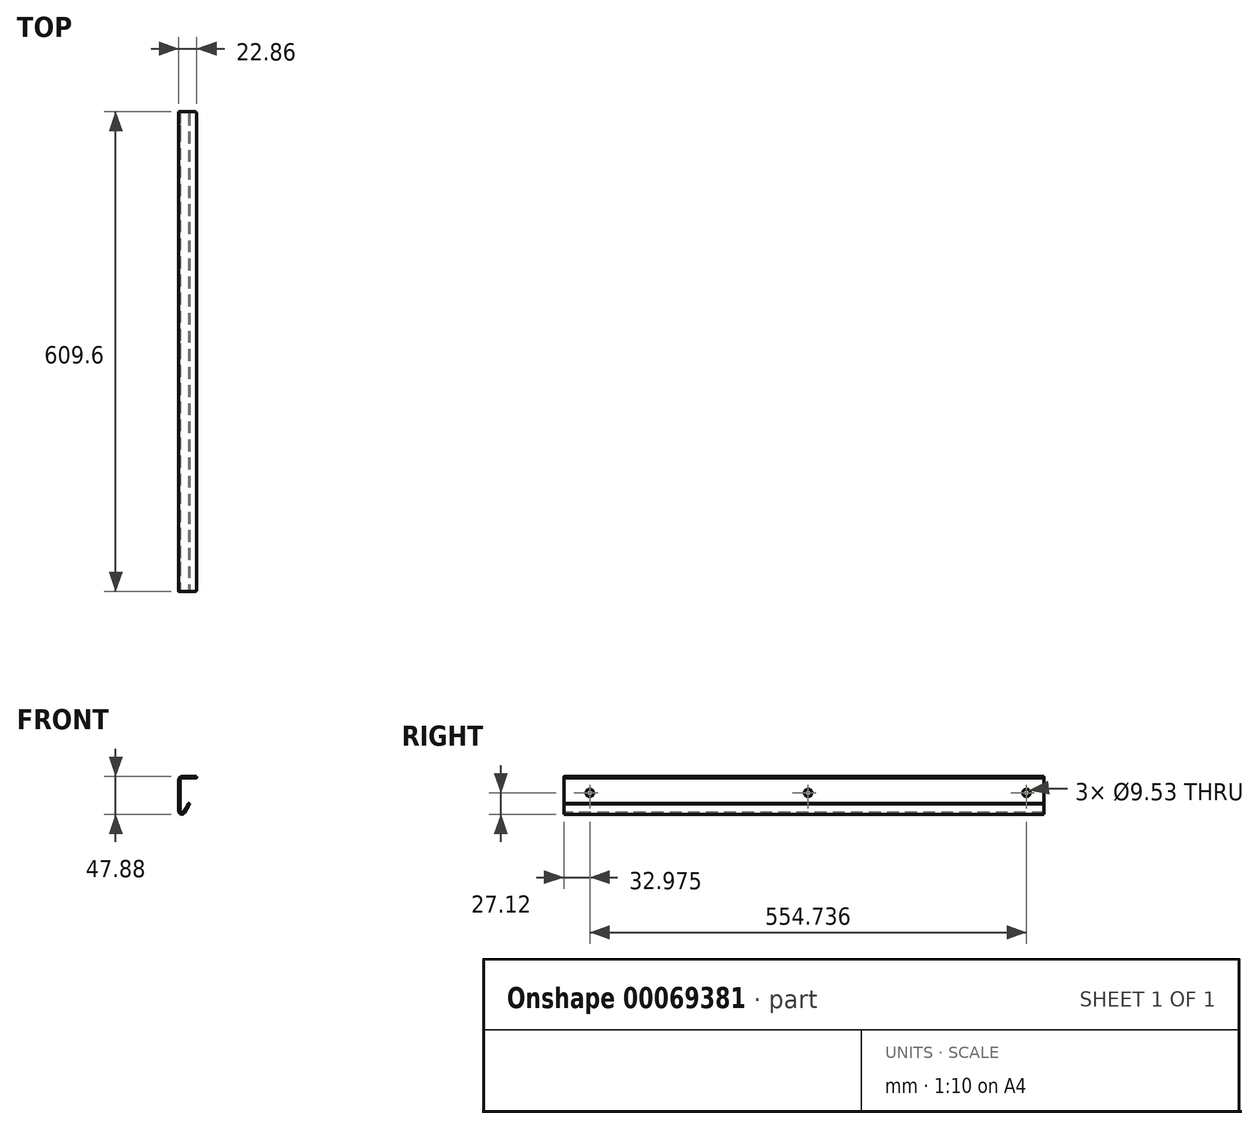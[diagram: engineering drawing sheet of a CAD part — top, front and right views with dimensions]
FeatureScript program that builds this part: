
annotation { "Feature Type Name" : "Feature", "Feature Type Description" : "" }
export const myFeature = defineFeature(function(context is Context, id is Id, definition is map)
    precondition{}
    {
        {
            var Q0;
            Q0=qCreatedBy(makeId("Front.planeOp"),FACE);
            var sketch = newSketch(context, id + "F0", { "sketchPlane" : qUnion([Q0])});
            skLineSegment(sketch, "E0", {"start": v(-1.41, 19.26) * mm, "end": v(-20.23, 19.26) * mm});
            skLineSegment(sketch, "E1", {"start": v(-22.77, 16.72) * mm, "end": v(-22.77, -22.45) * mm});
            skLineSegment(sketch, "E2", {"start": v(-18.03, -23.72) * mm, "end": v(-12.11, -13.47) * mm});
            skLineSegment(sketch, "E3.0", {"start": v(-17.16, -25.21) * mm, "end": v(-10.81, -14.21) * mm});
            skLineSegment(sketch, "E3.1", {"start": v(-24.27, 16.95) * mm, "end": v(-24.27, -23.3) * mm});
            skLineSegment(sketch, "E3.2", {"start": v(-1.41, 20.76) * mm, "end": v(-20.46, 20.76) * mm});
            skLineSegment(sketch, "E4", {"start": v(-10.81, -14.21) * mm, "end": v(-12.11, -13.47) * mm});
            skLineSegment(sketch, "E5", {"start": v(-1.41, 20.76) * mm, "end": v(-1.41, 19.26) * mm});
            skPoint(sketch, "E6.visualSharp", {"position": v(-22.77, 19.26) * mm});
            skArc(sketch, "E6.filletArc", {"start": v(-20.23, 19.26) * mm, "mid": v(-22.03, 18.52) * mm, "end": v(-22.77, 16.72) * mm});
            skPoint(sketch, "E7.visualSharp", {"position": v(-22.77, -31.93) * mm});
            skArc(sketch, "E7.filletArc", {"start": v(-22.77, -22.45) * mm, "mid": v(-20.9, -24.9) * mm, "end": v(-18.03, -23.72) * mm});
            skPoint(sketch, "E8.visualSharp", {"position": v(-24.27, -37.53) * mm});
            skArc(sketch, "E8.filletArc", {"start": v(-24.27, -23.3) * mm, "mid": v(-21.45, -26.99) * mm, "end": v(-17.16, -25.21) * mm});
            skPoint(sketch, "E9.visualSharp", {"position": v(-24.27, 20.76) * mm});
            skArc(sketch, "E9.filletArc", {"start": v(-20.46, 20.76) * mm, "mid": v(-23.16, 19.64) * mm, "end": v(-24.27, 16.95) * mm});
            skSolve(sketch);
        }
        {
            var Q0;
            Q0=qSketchRegion(id+"F0",true);
            extrude(context, id + "F1", {"entities" : qUnion([Q0]), "oppositeDirection" : true, "depth" : 609.6 * mm});
        }
        {
            var Q0;
            Q0=makeQuery(id+"F1.opExtrude","SWEPT_FACE",FACE,{"disambiguationData":[OSD([sQuery(id+"F0.wireOp",EDGE,"E3.2")])]});
            var sketch = newSketch(context, id + "F2", { "sketchPlane" : qUnion([Q0])});
            skCircle(sketch, "E10", {"center": v(-14.11, 12.7) * mm, "radius": 3.18 * mm});
            skCircle(sketch, "E11.0.1.0", {"center": v(-14.11, 38.1) * mm, "radius": 3.18 * mm});
            skCircle(sketch, "E11.0.2.0", {"center": v(-14.11, 63.5) * mm, "radius": 3.18 * mm});
            skCircle(sketch, "E11.0.3.0", {"center": v(-14.11, 88.9) * mm, "radius": 3.18 * mm});
            skCircle(sketch, "E11.0.4.0", {"center": v(-14.11, 114.3) * mm, "radius": 3.18 * mm});
            skCircle(sketch, "E11.0.5.0", {"center": v(-14.11, 139.7) * mm, "radius": 3.18 * mm});
            skCircle(sketch, "E11.0.6.0", {"center": v(-14.11, 165.1) * mm, "radius": 3.18 * mm});
            skCircle(sketch, "E11.0.7.0", {"center": v(-14.11, 190.5) * mm, "radius": 3.18 * mm});
            skCircle(sketch, "E11.0.8.0", {"center": v(-14.11, 215.9) * mm, "radius": 3.18 * mm});
            skCircle(sketch, "E11.0.9.0", {"center": v(-14.11, 241.3) * mm, "radius": 3.18 * mm});
            skCircle(sketch, "E11.0.10.0", {"center": v(-14.11, 266.7) * mm, "radius": 3.18 * mm});
            skCircle(sketch, "E11.0.11.0", {"center": v(-14.11, 292.1) * mm, "radius": 3.18 * mm});
            skCircle(sketch, "E11.0.12.0", {"center": v(-14.11, 317.5) * mm, "radius": 3.18 * mm});
            skCircle(sketch, "E11.0.13.0", {"center": v(-14.11, 342.9) * mm, "radius": 3.18 * mm});
            skCircle(sketch, "E11.0.14.0", {"center": v(-14.11, 368.3) * mm, "radius": 3.18 * mm});
            skCircle(sketch, "E11.0.15.0", {"center": v(-14.11, 393.7) * mm, "radius": 3.18 * mm});
            skCircle(sketch, "E11.0.16.0", {"center": v(-14.11, 419.1) * mm, "radius": 3.18 * mm});
            skCircle(sketch, "E11.0.17.0", {"center": v(-14.11, 444.5) * mm, "radius": 3.18 * mm});
            skLineSegment(sketch, "E11.direction1", {"start": v(-14.11, 12.7) * mm, "end": v(24.77, 12.7) * mm, "construction": true});
            skLineSegment(sketch, "E11.direction2", {"start": v(-14.11, 12.7) * mm, "end": v(-14.11, 38.1) * mm, "construction": true});
            skCircle(sketch, "E12.0.0.18", {"center": v(-14.11, 469.9) * mm, "radius": 3.18 * mm});
            skCircle(sketch, "E12.0.0.19", {"center": v(-14.11, 495.3) * mm, "radius": 3.18 * mm});
            skCircle(sketch, "E12.0.0.20", {"center": v(-14.11, 520.7) * mm, "radius": 3.18 * mm});
            skCircle(sketch, "E12.0.0.21", {"center": v(-14.11, 546.1) * mm, "radius": 3.18 * mm});
            skCircle(sketch, "E12.0.0.22", {"center": v(-14.11, 571.5) * mm, "radius": 3.18 * mm});
            skCircle(sketch, "E12.0.0.23", {"center": v(-14.11, 596.9) * mm, "radius": 3.18 * mm});
            skSolve(sketch);
        }
        {
            var Q0;
            Q0=makeQuery(id+"F1.opExtrude","CAP_EDGE",EDGE,{"disambiguationData":[OSD([sQuery(id+"F0.wireOp",EDGE,"E5")])],"isStart":true});
            var Q1;
            Q1=makeQuery(id+"F1.opExtrude","CAP_EDGE",EDGE,{"disambiguationData":[OSD([sQuery(id+"F0.wireOp",EDGE,"E4")])],"isStart":true});
            var Q2;
            Q2=makeQuery(id+"F1.opExtrude","CAP_EDGE",EDGE,{"disambiguationData":[OSD([sQuery(id+"F0.wireOp",EDGE,"E4")])],"isStart":false});
            var Q3;
            Q3=makeQuery(id+"F1.opExtrude","CAP_EDGE",EDGE,{"disambiguationData":[OSD([sQuery(id+"F0.wireOp",EDGE,"E5")])],"isStart":false});
            fillet(context, id + "F3", {"entities" : qUnion([Q0, Q1, Q2, Q3]), "radius" : 2.54 * mm, "tangentPropagation" : true});
        }
        {
            var Q0;
            Q0=makeQuery(id+"F1.opExtrude","SWEPT_FACE",FACE,{"disambiguationData":[OSD([sQuery(id+"F0.wireOp",EDGE,"E1")])]});
            var sketch = newSketch(context, id + "F4", { "sketchPlane" : qUnion([Q0])});
            skCircle(sketch, "E13", {"center": v(32.97, 0) * mm, "radius": 4.76 * mm});
            skCircle(sketch, "E14.1.0.0", {"center": v(310.34, 0) * mm, "radius": 4.76 * mm});
            skCircle(sketch, "E14.2.0.0", {"center": v(587.71, 0) * mm, "radius": 4.76 * mm});
            skLineSegment(sketch, "E14.direction1", {"start": v(32.97, 0) * mm, "end": v(310.34, 0) * mm, "construction": true});
            skSolve(sketch);
        }
        {
            var Q0;
            Q0=makeQuery(id+"F4.imprint","IMPRINT",FACE,{"disambiguationData":[TD([[makeQuery(id+"F4.imprint","IMPRINT",EDGE,{"derivedFrom":sQuery(id+"F4.wireOp",EDGE,"E13")}),1.0]])]});
            var Q1;
            Q1=makeQuery(id+"F4.imprint","IMPRINT",FACE,{"disambiguationData":[TD([[makeQuery(id+"F4.imprint","IMPRINT",EDGE,{"derivedFrom":sQuery(id+"F4.wireOp",EDGE,"E14.1.0.0")}),1.0]])]});
            var Q2;
            Q2=makeQuery(id+"F4.imprint","IMPRINT",FACE,{"disambiguationData":[TD([[makeQuery(id+"F4.imprint","IMPRINT",EDGE,{"derivedFrom":sQuery(id+"F4.wireOp",EDGE,"E14.2.0.0")}),1.0]])]});
            extrude(context, id + "F5", {"entities" : qUnion([Q0, Q1, Q2]), "operationType" : NewBodyOperationType.REMOVE, "oppositeDirection" : true, "depth" : 25.4 * mm, "offsetDistance" : 25.4 * mm});
        }
    });
